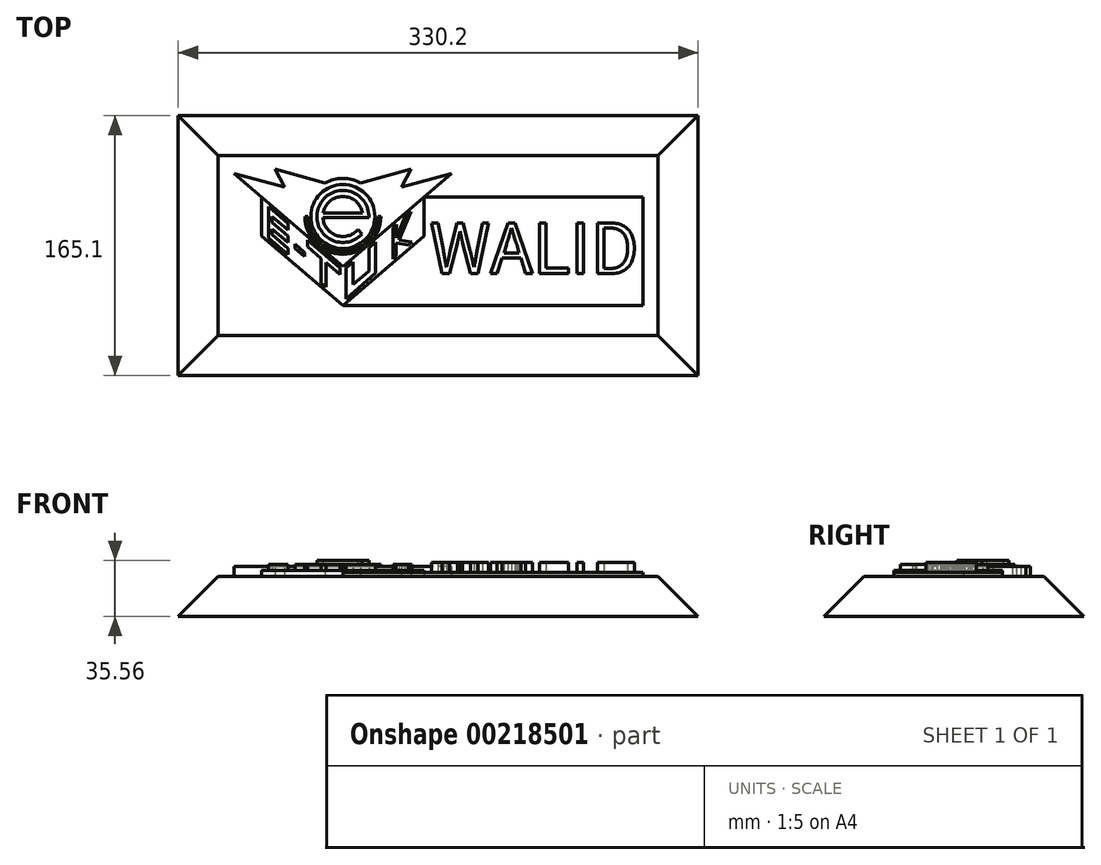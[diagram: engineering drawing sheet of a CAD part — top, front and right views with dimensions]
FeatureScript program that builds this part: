
annotation { "Feature Type Name" : "Feature", "Feature Type Description" : "" }
export const myFeature = defineFeature(function(context is Context, id is Id, definition is map)
    precondition{}
    {
        {
            var Q0;
            Q0=qCreatedBy(makeId("Top.planeOp"),FACE);
            var sketch = newSketch(context, id + "F0", { "sketchPlane" : qUnion([Q0])});
            skArc(sketch, "E0", {"start": v(12.53, 2.07) * mm, "mid": v(0, 12.7) * mm, "end": v(-12.53, 2.07) * mm});
            skArc(sketch, "E1", {"start": v(16.5, -0.78) * mm, "mid": v(-15.23, 6.37) * mm, "end": v(12.14, -11.18) * mm});
            skLineSegment(sketch, "E2", {"start": v(12.7, -0.78) * mm, "end": v(-12.68, -0.78) * mm});
            skLineSegment(sketch, "E3", {"start": v(-12.68, -0.78) * mm, "end": v(16.5, -0.78) * mm});
            skLineSegment(sketch, "E4", {"start": v(9.59, -8.33) * mm, "end": v(12.14, -11.18) * mm});
            skArc(sketch, "E5.trimOffspring", {"start": v(-12.68, -0.78) * mm, "mid": v(-4.08, -12.03) * mm, "end": v(9.59, -8.33) * mm});
            skLineSegment(sketch, "E6", {"start": v(-12.53, 2.07) * mm, "end": v(12.53, 2.07) * mm});
            skSolve(sketch);
        }
        {
            var Q0;
            Q0=makeQuery(id+"F0.imprint","IMPRINT",FACE,{"disambiguationData":[TD([[makeQuery(id+"F0.imprint","IMPRINT",EDGE,{"derivedFrom":sQuery(id+"F0.wireOp",EDGE,"E0")}),-1.0]])]});
            extrude(context, id + "F1", {"entities" : qUnion([Q0]), "depth" : 10.16 * mm});
        }
        {
            var Q0;
            Q0=qCreatedBy(makeId("Top.planeOp"),FACE);
            var sketch = newSketch(context, id + "F2", { "sketchPlane" : qUnion([Q0])});
            skCircle(sketch, "E7", {"center": v(0, 0) * mm, "radius": 20.32 * mm});
            skSolve(sketch);
        }
        {
            var Q0;
            Q0=qSketchRegion(id+"F2",true);
            extrude(context, id + "F3", {"entities" : qUnion([Q0]), "operationType" : NewBodyOperationType.ADD, "depth" : 7.62 * mm});
        }
        {
            var Q0;
            Q0=qCreatedBy(makeId("Top.planeOp"),FACE);
            var sketch = newSketch(context, id + "F4", { "sketchPlane" : qUnion([Q0])});
            skLineSegment(sketch, "E8", {"start": v(-69.02, 27.27) * mm, "end": v(-37.13, 18.72) * mm});
            skLineSegment(sketch, "E9", {"start": v(-37.13, 18.72) * mm, "end": v(-43.14, 30.14) * mm});
            skLineSegment(sketch, "E10", {"start": v(-43.14, 30.14) * mm, "end": v(-11.32, 21.31) * mm});
            skLineSegment(sketch, "E11", {"start": v(-69.02, 27.27) * mm, "end": v(0, -31.75) * mm});
            skLineSegment(sketch, "E12.MirrorCS", {"start": v(43.14, 30.14) * mm, "end": v(11.32, 21.31) * mm});
            skLineSegment(sketch, "E13.MirrorCS", {"start": v(69.02, 27.27) * mm, "end": v(0, -31.75) * mm});
            skLineSegment(sketch, "E14.MirrorCS", {"start": v(69.02, 27.27) * mm, "end": v(37.13, 18.72) * mm});
            skLineSegment(sketch, "E15.MirrorCS", {"start": v(37.13, 18.72) * mm, "end": v(43.14, 30.14) * mm});
            skArc(sketch, "E16.trimOffspring", {"start": v(11.32, 21.31) * mm, "mid": v(0, 24.13) * mm, "end": v(-11.32, 21.31) * mm});
            skSolve(sketch);
        }
        {
            var Q0;
            Q0=qSketchRegion(id+"F4",true);
            var Q1;
            Q1=makeQuery(id+"F2.imprint","IMPRINT",FACE,{"disambiguationData":[TD([[makeQuery(id+"F2.imprint","IMPRINT",EDGE,{"derivedFrom":sQuery(id+"F2.wireOp",EDGE,"E7")}),1.0]])]});
            extrude(context, id + "F5", {"entities" : qUnion([Q0, Q1]), "operationType" : NewBodyOperationType.ADD, "depth" : 6.35 * mm});
        }
        {
            var Q0;
            Q0=qCreatedBy(makeId("Top.planeOp"),FACE);
            var sketch = newSketch(context, id + "F6", { "sketchPlane" : qUnion([Q0])});
            skLineSegment(sketch, "E17", {"start": v(-51.6, -12.38) * mm, "end": v(0, -56.51) * mm});
            skLineSegment(sketch, "E18", {"start": v(0, -56.51) * mm, "end": v(51.6, -12.38) * mm});
            skLineSegment(sketch, "E19", {"start": v(-51.6, 12.38) * mm, "end": v(-51.6, -12.38) * mm});
            skLineSegment(sketch, "E20", {"start": v(51.6, 12.38) * mm, "end": v(51.6, -12.38) * mm});
            skLineSegment(sketch, "E21", {"start": v(-51.6, 12.38) * mm, "end": v(0, -31.75) * mm});
            skLineSegment(sketch, "E22", {"start": v(0, -31.75) * mm, "end": v(51.6, 12.38) * mm});
            skSolve(sketch);
        }
        {
            var Q0;
            Q0=qSketchRegion(id+"F6",true);
            extrude(context, id + "F7", {"entities" : qUnion([Q0]), "operationType" : NewBodyOperationType.ADD, "depth" : 3.8 * mm});
        }
        {
            var Q0;
            Q0=makeQuery(id+"F7.opExtrude","CAP_FACE",FACE,{"disambiguationData":[OSD([sQuery(id+"F6.wireOp",EDGE,"E17"),sQuery(id+"F6.wireOp",EDGE,"E18"),sQuery(id+"F6.wireOp",EDGE,"E19"),sQuery(id+"F6.wireOp",EDGE,"E20"),sQuery(id+"F6.wireOp",EDGE,"E21"),sQuery(id+"F6.wireOp",EDGE,"E22")])],"isStart":false});
            var sketch = newSketch(context, id + "F8", { "sketchPlane" : qUnion([Q0])});
            skPoint(sketch, "E23.startSnap0", {"position": v(-51.6, 0) * mm});
            skLineSegment(sketch, "E24", {"start": v(-51.6, -9.87) * mm, "end": v(-51.6, 9.87) * mm, "construction": true});
            skLineSegment(sketch, "E25", {"start": v(-47.26, 6.16) * mm, "end": v(-34.74, -4.55) * mm});
            skLineSegment(sketch, "E26", {"start": v(-34.74, -4.55) * mm, "end": v(-34.74, -8.63) * mm});
            skLineSegment(sketch, "E27", {"start": v(-34.74, -8.63) * mm, "end": v(-44.83, 0) * mm});
            skLineSegment(sketch, "E28", {"start": v(-44.83, 0) * mm, "end": v(-44.83, -3.75) * mm});
            skLineSegment(sketch, "E29", {"start": v(-44.83, -3.75) * mm, "end": v(-34.74, -12.38) * mm});
            skLineSegment(sketch, "E30", {"start": v(-34.74, -12.38) * mm, "end": v(-34.74, -16.46) * mm});
            skLineSegment(sketch, "E31", {"start": v(-34.74, -16.46) * mm, "end": v(-44.83, -7.83) * mm});
            skLineSegment(sketch, "E32", {"start": v(-44.83, -7.83) * mm, "end": v(-44.83, -11.58) * mm});
            skLineSegment(sketch, "E33", {"start": v(-44.83, -11.58) * mm, "end": v(-34.74, -20.21) * mm});
            skLineSegment(sketch, "E34", {"start": v(-34.74, -20.21) * mm, "end": v(-34.74, -24.3) * mm});
            skLineSegment(sketch, "E35", {"start": v(-34.74, -24.3) * mm, "end": v(-47.26, -13.59) * mm});
            skLineSegment(sketch, "E36", {"start": v(-47.26, 6.16) * mm, "end": v(-47.26, -13.59) * mm});
            skLineSegment(sketch, "E37", {"start": v(-30.38, -20.21) * mm, "end": v(-30.38, -17.65) * mm});
            skLineSegment(sketch, "E38", {"start": v(-30.38, -17.65) * mm, "end": v(-24.17, -22.96) * mm});
            skLineSegment(sketch, "E39", {"start": v(-24.17, -22.96) * mm, "end": v(-24.17, -25.53) * mm});
            skLineSegment(sketch, "E40", {"start": v(-24.17, -25.53) * mm, "end": v(-30.38, -20.21) * mm});
            skLineSegment(sketch, "E41", {"start": v(-22.38, -15.12) * mm, "end": v(-1.9, -32.63) * mm});
            skLineSegment(sketch, "E42", {"start": v(-1.9, -32.63) * mm, "end": v(-1.9, -36.71) * mm});
            skLineSegment(sketch, "E43", {"start": v(-1.9, -36.71) * mm, "end": v(-10.6, -29.28) * mm});
            skLineSegment(sketch, "E44", {"start": v(-10.6, -29.28) * mm, "end": v(-10.6, -44.95) * mm});
            skLineSegment(sketch, "E45", {"start": v(-10.6, -44.95) * mm, "end": v(-13.7, -42.3) * mm});
            skLineSegment(sketch, "E46", {"start": v(-13.7, -42.3) * mm, "end": v(-13.7, -26.63) * mm});
            skLineSegment(sketch, "E47", {"start": v(-13.7, -26.63) * mm, "end": v(-22.38, -19.2) * mm});
            skLineSegment(sketch, "E48", {"start": v(-22.38, -19.2) * mm, "end": v(-22.38, -15.12) * mm});
            skLineSegment(sketch, "E49", {"start": v(1.9, -32.62) * mm, "end": v(6.3, -28.86) * mm});
            skLineSegment(sketch, "E50", {"start": v(6.3, -28.86) * mm, "end": v(6.3, -43.26) * mm});
            skLineSegment(sketch, "E51", {"start": v(6.3, -43.26) * mm, "end": v(16.5, -34.54) * mm});
            skLineSegment(sketch, "E52", {"start": v(16.5, -34.54) * mm, "end": v(16.5, -20.14) * mm});
            skLineSegment(sketch, "E53", {"start": v(16.5, -20.14) * mm, "end": v(20.85, -16.3) * mm});
            skLineSegment(sketch, "E54", {"start": v(20.85, -16.3) * mm, "end": v(20.85, -36.06) * mm});
            skLineSegment(sketch, "E55", {"start": v(20.85, -36.06) * mm, "end": v(1.9, -52.37) * mm});
            skLineSegment(sketch, "E56", {"start": v(1.9, -52.37) * mm, "end": v(1.9, -32.62) * mm});
            skLineSegment(sketch, "E57", {"start": v(31.73, -7.12) * mm, "end": v(31.73, -27.15) * mm});
            skLineSegment(sketch, "E58", {"start": v(31.73, -27.15) * mm, "end": v(33.91, -25.22) * mm});
            skLineSegment(sketch, "E59", {"start": v(33.91, -25.22) * mm, "end": v(33.91, -16.82) * mm});
            skLineSegment(sketch, "E60", {"start": v(33.94, -13.64) * mm, "end": v(33.94, -5.23) * mm});
            skLineSegment(sketch, "E61", {"start": v(33.94, -5.23) * mm, "end": v(31.73, -7.12) * mm});
            skLineSegment(sketch, "E62", {"start": v(41.79, -18.27) * mm, "end": v(44, -16.38) * mm});
            skLineSegment(sketch, "E63", {"start": v(33.94, -13.64) * mm, "end": v(39.5, 0) * mm});
            skLineSegment(sketch, "E64", {"start": v(33.91, -16.82) * mm, "end": v(41.79, -18.27) * mm});
            skLineSegment(sketch, "E65", {"start": v(44, -16.38) * mm, "end": v(35.85, -14.87) * mm});
            skLineSegment(sketch, "E66", {"start": v(35.85, -14.87) * mm, "end": v(43.2, 3.16) * mm});
            skLineSegment(sketch, "E67", {"start": v(39.5, 0) * mm, "end": v(43.2, 3.16) * mm});
            skSolve(sketch);
        }
        {
            var Q0;
            Q0=qSketchRegion(id+"F8",true);
            extrude(context, id + "F9", {"entities" : qUnion([Q0]), "operationType" : NewBodyOperationType.ADD, "depth" : 3.8 * mm});
        }
        {
            var Q0;
            Q0=makeQuery(id+"F5.boolean.opBoolean","MERGE",FACE,{"derivedFrom":[makeQuery(id+"F5.opExtrude","CAP_FACE",FACE,{"disambiguationData":[OSD([sQuery(id+"F2.wireOp",EDGE,"E7")])],"isStart":false}),makeQuery(id+"F5.opExtrude","CAP_FACE",FACE,{"disambiguationData":[OSD([sQuery(id+"F4.wireOp",EDGE,"E8"),sQuery(id+"F4.wireOp",EDGE,"E9"),sQuery(id+"F4.wireOp",EDGE,"E10"),sQuery(id+"F4.wireOp",EDGE,"E11"),sQuery(id+"F4.wireOp",EDGE,"E13.MirrorCS"),sQuery(id+"F4.wireOp",EDGE,"E14.MirrorCS"),sQuery(id+"F4.wireOp",EDGE,"E12.MirrorCS"),sQuery(id+"F4.wireOp",EDGE,"E15.MirrorCS"),sQuery(id+"F4.wireOp",EDGE,"E16.trimOffspring")])],"isStart":false})]});
            var sketch = newSketch(context, id + "F10", { "sketchPlane" : qUnion([Q0])});
            skArc(sketch, "E68", {"start": v(-24.13, 0) * mm, "mid": v(0, -24.13) * mm, "end": v(24.13, 0) * mm});
            skArc(sketch, "E69", {"start": v(-22.23, 0) * mm, "mid": v(0, -22.23) * mm, "end": v(22.23, 0) * mm});
            skLineSegment(sketch, "E70", {"start": v(-24.13, 0) * mm, "end": v(-22.23, 0) * mm});
            skLineSegment(sketch, "E71", {"start": v(24.13, 0) * mm, "end": v(22.23, 0) * mm});
            skSolve(sketch);
        }
        {
            var Q0;
            Q0=qSketchRegion(id+"F10",true);
            extrude(context, id + "F11", {"entities" : qUnion([Q0]), "operationType" : NewBodyOperationType.ADD, "depth" : 1.27 * mm});
        }
        {
            var Q0;
            {var subQ0=sQuery(id+"F2.wireOp",EDGE,"E7");Q0=makeQuery(id+"F7.boolean.opBoolean","MERGE",FACE,{"derivedFrom":[makeQuery(id+"F5.boolean.opBoolean","MERGE",FACE,{"derivedFrom":[makeQuery(id+"F3.boolean.opBoolean","MERGE",FACE,{"derivedFrom":[makeQuery(id+"F1.opExtrude","CAP_FACE",FACE,{"disambiguationData":[OSD([sQuery(id+"F0.wireOp",EDGE,"E0"),sQuery(id+"F0.wireOp",EDGE,"E1"),sQuery(id+"F0.wireOp",EDGE,"E3"),sQuery(id+"F0.wireOp",EDGE,"E4"),sQuery(id+"F0.wireOp",EDGE,"E5.trimOffspring"),sQuery(id+"F0.wireOp",EDGE,"E6")])],"isStart":true}),makeQuery(id+"F3.opExtrude","CAP_FACE",FACE,{"disambiguationData":[OSD([subQ0])],"isStart":true})]}),makeQuery(id+"F5.opExtrude","CAP_FACE",FACE,{"disambiguationData":[OSD([subQ0])],"isStart":true}),makeQuery(id+"F5.opExtrude","CAP_FACE",FACE,{"disambiguationData":[OSD([sQuery(id+"F4.wireOp",EDGE,"E8"),sQuery(id+"F4.wireOp",EDGE,"E9"),sQuery(id+"F4.wireOp",EDGE,"E10"),sQuery(id+"F4.wireOp",EDGE,"E11"),sQuery(id+"F4.wireOp",EDGE,"E13.MirrorCS"),sQuery(id+"F4.wireOp",EDGE,"E14.MirrorCS"),sQuery(id+"F4.wireOp",EDGE,"E12.MirrorCS"),sQuery(id+"F4.wireOp",EDGE,"E15.MirrorCS"),sQuery(id+"F4.wireOp",EDGE,"E16.trimOffspring")])],"isStart":true})]}),makeQuery(id+"F7.opExtrude","CAP_FACE",FACE,{"disambiguationData":[OSD([sQuery(id+"F6.wireOp",EDGE,"E17"),sQuery(id+"F6.wireOp",EDGE,"E18"),sQuery(id+"F6.wireOp",EDGE,"E19"),sQuery(id+"F6.wireOp",EDGE,"E20"),sQuery(id+"F6.wireOp",EDGE,"E21"),sQuery(id+"F6.wireOp",EDGE,"E22")])],"isStart":true})]});}
            var sketch = newSketch(context, id + "F12", { "sketchPlane" : qUnion([Q0])});
            skLineSegment(sketch, "E72.bottom", {"start": v(0, 56.51) * mm, "end": v(190.5, 56.51) * mm});
            skLineSegment(sketch, "E72.right", {"start": v(190.5, 56.51) * mm, "end": v(190.5, -12.38) * mm});
            skLineSegment(sketch, "E73", {"start": v(51.6, -12.38) * mm, "end": v(190.5, -12.38) * mm});
            skLineSegment(sketch, "E74", {"start": v(0, 56.51) * mm, "end": v(51.6, 12.38) * mm});
            skLineSegment(sketch, "E75", {"start": v(51.6, 12.38) * mm, "end": v(51.6, -12.38) * mm});
            skSolve(sketch);
        }
        {
            var Q0;
            Q0=qSketchRegion(id+"F12",true);
            extrude(context, id + "F13", {"entities" : qUnion([Q0]), "operationType" : NewBodyOperationType.ADD, "oppositeDirection" : true, "depth" : 2.54 * mm});
        }
        {
            var Q0;
            Q0=makeQuery(id+"F13.opExtrude","CAP_FACE",FACE,{"disambiguationData":[OSD([sQuery(id+"F12.wireOp",EDGE,"E72.bottom"),sQuery(id+"F12.wireOp",EDGE,"E72.right"),sQuery(id+"F12.wireOp",EDGE,"E73"),sQuery(id+"F12.wireOp",EDGE,"E74"),sQuery(id+"F12.wireOp",EDGE,"E75")])],"isStart":false});
            var sketch = newSketch(context, id + "F14", { "sketchPlane" : qUnion([Q0])});
            skLineSegment(sketch, "E76", {"start": v(51.6, 12.38) * mm, "end": v(51.6, -56.51) * mm, "construction": true});
            skLineSegment(sketch, "E77", {"start": v(51.6, -56.51) * mm, "end": v(190.5, -56.51) * mm, "construction": true});
            skLineSegment(sketch, "E78", {"start": v(190.5, -56.51) * mm, "end": v(190.5, 12.38) * mm, "construction": true});
            skLineSegment(sketch, "E79", {"start": v(190.5, 12.38) * mm, "end": v(51.6, 12.38) * mm, "construction": true});
            skPoint(sketch, "E80.startSnap0", {"position": v(51.6, 0) * mm});
            skPoint(sketch, "E80.endSnap0", {"position": v(51.6, 0) * mm});
            skLineSegment(sketch, "E81", {"start": v(187.62, -36.36) * mm, "end": v(55.06, -36.36) * mm, "construction": true});
            skLineSegment(sketch, "E82", {"start": v(178.12, -4.6) * mm, "end": v(55.06, -4.6) * mm, "construction": true});
            skText(sketch, "E83", { "text": "WALID", "fontName": "NotoSansCJKkr-Regular.otf"});
            const initialGuessF14  = {"E83": [0.05506, -0.03636, 1, 0, 0.03175]};
            skSetInitialGuess(sketch, initialGuessF14);
            skSolve(sketch);
        }
        {
            var Q0;
            Q0=qSketchRegion(id+"F14",true);
            extrude(context, id + "F15", {"entities" : qUnion([Q0]), "operationType" : NewBodyOperationType.ADD, "depth" : 6.35 * mm});
        }
        {
            var Q0;
            Q0=makeQuery(id+"F13.opExtrude","CAP_FACE",FACE,{"disambiguationData":[OSD([sQuery(id+"F12.wireOp",EDGE,"E72.bottom"),sQuery(id+"F12.wireOp",EDGE,"E72.right"),sQuery(id+"F12.wireOp",EDGE,"E73"),sQuery(id+"F12.wireOp",EDGE,"E74"),sQuery(id+"F12.wireOp",EDGE,"E75")])],"isStart":true});
            var sketch = newSketch(context, id + "F16", { "sketchPlane" : qUnion([Q0])});
            skLineSegment(sketch, "E84.bottom", {"start": v(-79.18, -38.74) * mm, "end": v(200.22, -38.74) * mm});
            skLineSegment(sketch, "E84.top", {"start": v(-79.18, 75.56) * mm, "end": v(200.22, 75.56) * mm});
            skLineSegment(sketch, "E84.left", {"start": v(-79.18, -38.74) * mm, "end": v(-79.18, 75.56) * mm});
            skLineSegment(sketch, "E84.right", {"start": v(200.22, -38.74) * mm, "end": v(200.22, 75.56) * mm});
            skSolve(sketch);
        }
        {
            var Q0;
            Q0=qSketchRegion(id+"F16",true);
            extrude(context, id + "F17", {"entities" : qUnion([Q0]), "operationType" : NewBodyOperationType.ADD, "depth" : 25.4 * mm, "hasDraft" : true, "draftAngle" : 45 * degree});
        }
    });
